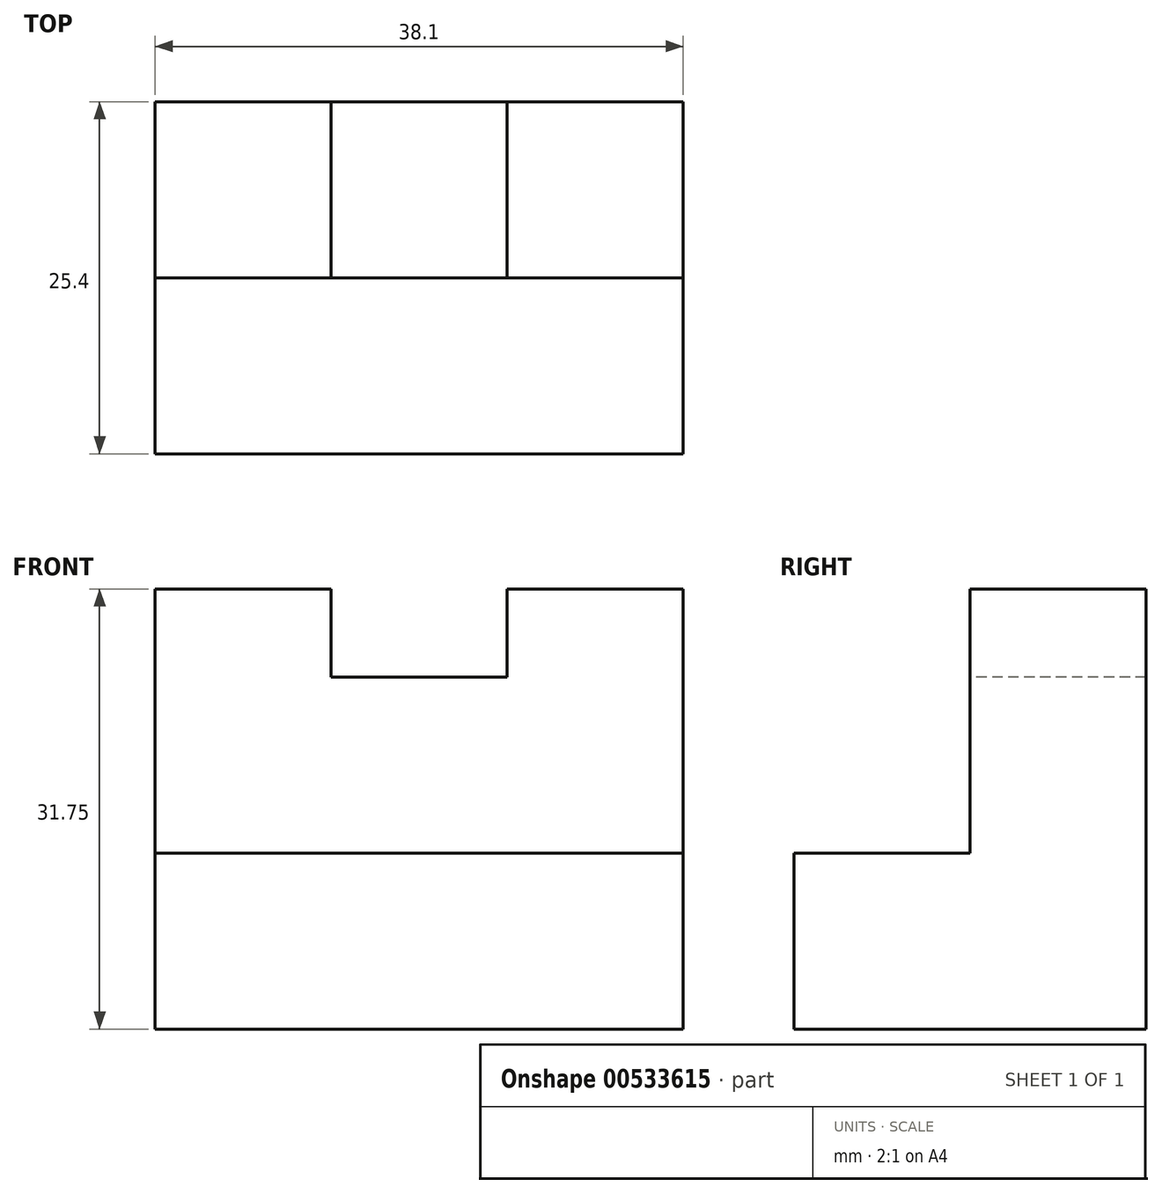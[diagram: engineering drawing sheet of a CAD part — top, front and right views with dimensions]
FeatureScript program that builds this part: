
annotation { "Feature Type Name" : "Feature", "Feature Type Description" : "" }
export const myFeature = defineFeature(function(context is Context, id is Id, definition is map)
    precondition{}
    {
        {
            var Q0;
            Q0=qCreatedBy(makeId("Right.planeOp"),FACE);
            var sketch = newSketch(context, id + "F0", { "sketchPlane" : qUnion([Q0])});
            skLineSegment(sketch, "E0", {"start": v(-58.55, 51.3) * mm, "end": v(-45.85, 51.3) * mm});
            skLineSegment(sketch, "E1", {"start": v(-45.85, 51.3) * mm, "end": v(-45.85, 19.56) * mm});
            skLineSegment(sketch, "E2", {"start": v(-45.85, 19.56) * mm, "end": v(-71.25, 19.56) * mm});
            skLineSegment(sketch, "E3", {"start": v(-71.25, 19.56) * mm, "end": v(-71.25, 32.26) * mm});
            skLineSegment(sketch, "E4", {"start": v(-71.25, 32.26) * mm, "end": v(-58.55, 32.26) * mm});
            skLineSegment(sketch, "E5", {"start": v(-58.55, 51.3) * mm, "end": v(-58.55, 32.26) * mm});
            skSolve(sketch);
        }
        {
            var Q0;
            Q0=makeQuery(id+"F0.imprint","IMPRINT",FACE,{"disambiguationData":[TD([[makeQuery(id+"F0.imprint","IMPRINT",EDGE,{"derivedFrom":sQuery(id+"F0.wireOp",EDGE,"E0")}),-1.0]])]});
            extrude(context, id + "F1", {"entities" : qUnion([Q0]), "depth" : 25.4 * mm, "offsetDistance" : 25.4 * mm});
        }
        {
            var Q0;
            Q0=makeQuery(id+"F1.opExtrude","CAP_FACE",FACE,{"disambiguationData":[OSD([sQuery(id+"F0.wireOp",EDGE,"E0"),sQuery(id+"F0.wireOp",EDGE,"E1"),sQuery(id+"F0.wireOp",EDGE,"E2"),sQuery(id+"F0.wireOp",EDGE,"E3"),sQuery(id+"F0.wireOp",EDGE,"E4"),sQuery(id+"F0.wireOp",EDGE,"E5")])],"isStart":false});
            extrude(context, id + "F2", {"entities" : qUnion([Q0]), "operationType" : NewBodyOperationType.ADD, "depth" : 12.7 * mm, "offsetDistance" : 25.4 * mm});
        }
        {
            var Q0;
            {var subQ0=sQuery(id+"F0.wireOp",EDGE,"E5");Q0=makeQuery(id+"F2.boolean.opBoolean","MERGE",FACE,{"derivedFrom":[makeQuery(id+"F1.opExtrude","SWEPT_FACE",FACE,{"disambiguationData":[OSD([subQ0])]}),makeQuery(id+"F2.opExtrude","SWEPT_FACE",FACE,{"disambiguationData":[OSD([subQ0])]})]});}
            var sketch = newSketch(context, id + "F3", { "sketchPlane" : qUnion([Q0])});
            skLineSegment(sketch, "E6", {"start": v(12.7, 51.3) * mm, "end": v(12.7, 44.96) * mm});
            skLineSegment(sketch, "E7", {"start": v(12.7, 44.96) * mm, "end": v(25.4, 44.96) * mm});
            skLineSegment(sketch, "E8", {"start": v(25.4, 44.96) * mm, "end": v(25.4, 51.3) * mm});
            skSolve(sketch);
        }
        {
            var Q0;
            {var subQ0=sQuery(id+"F3.wireOp",EDGE,"E6");Q0=makeQuery(id+"F3.imprint","IMPRINT",FACE,{"disambiguationData":[TD([[makeQuery(id+"F3.imprint","IMPRINT",EDGE,{"derivedFrom":subQ0}),1.0]])]});}
            extrude(context, id + "F4", {"entities" : qUnion([Q0]), "operationType" : NewBodyOperationType.REMOVE, "endBound" : BoundingType.THROUGH_ALL, "oppositeDirection" : true, "depth" : 25.4 * mm, "offsetDistance" : 25.4 * mm});
        }
    });
